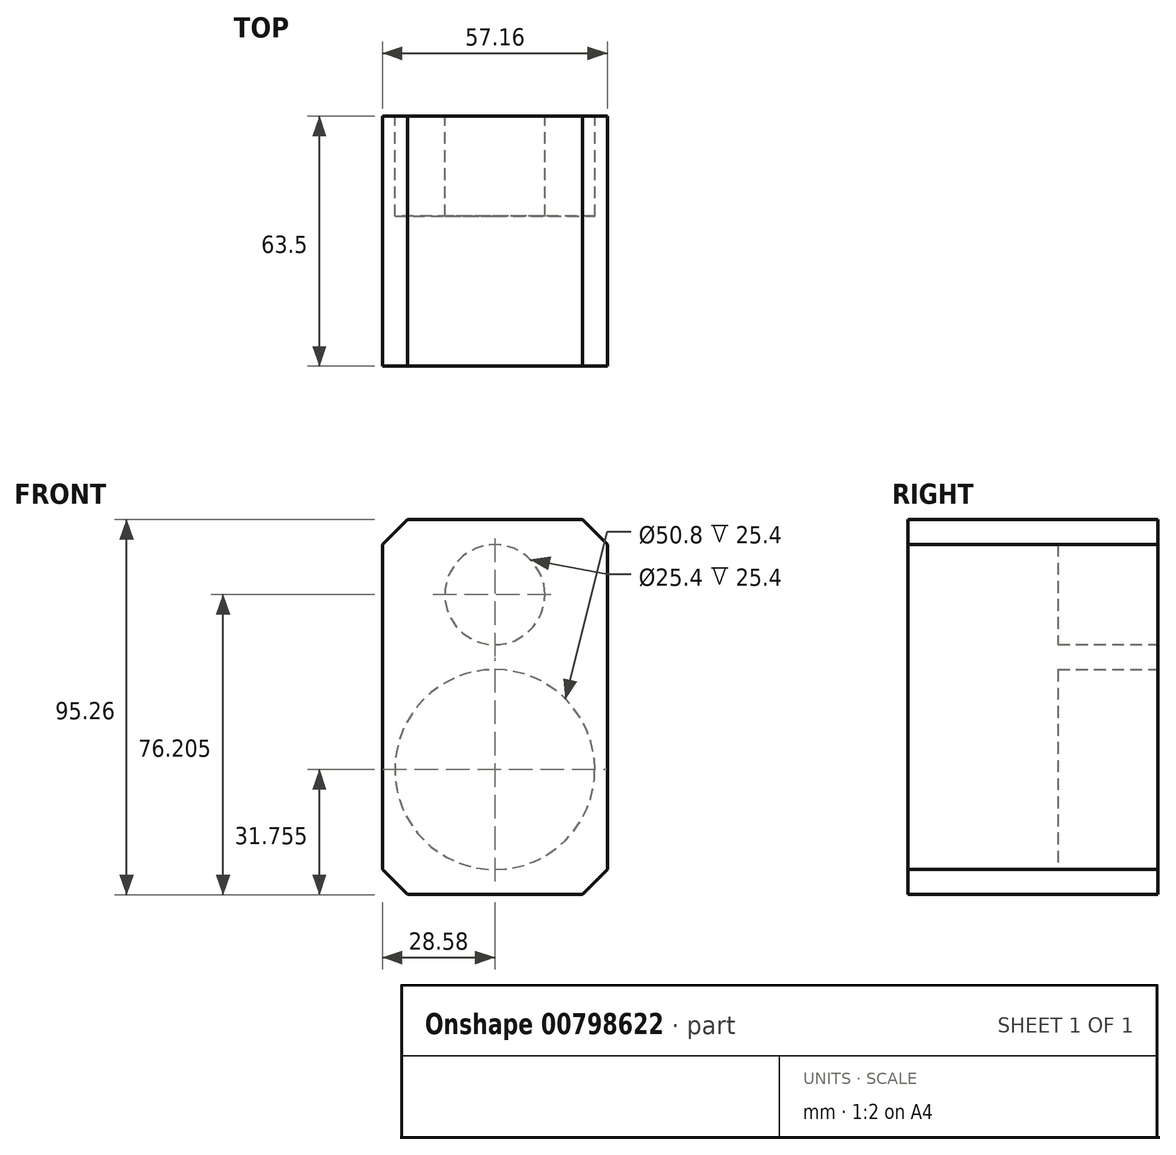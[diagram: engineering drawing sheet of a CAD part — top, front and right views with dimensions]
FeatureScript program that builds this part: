
annotation { "Feature Type Name" : "Feature", "Feature Type Description" : "" }
export const myFeature = defineFeature(function(context is Context, id is Id, definition is map)
    precondition{}
    {
        {
            var Q0;
            Q0=qCreatedBy(makeId("Front.planeOp"),FACE);
            var sketch = newSketch(context, id + "F0", { "sketchPlane" : qUnion([Q0])});
            skLineSegment(sketch, "E0.bottom", {"start": v(28.58, 47.63) * mm, "end": v(-28.58, 47.63) * mm});
            skLineSegment(sketch, "E0.top", {"start": v(28.58, -47.62) * mm, "end": v(-28.58, -47.62) * mm});
            skLineSegment(sketch, "E0.left", {"start": v(28.58, 47.63) * mm, "end": v(28.58, -47.62) * mm});
            skLineSegment(sketch, "E0.right", {"start": v(-28.58, 47.63) * mm, "end": v(-28.58, -47.62) * mm});
            skPoint(sketch, "E0.middle", {"position": v(0, 0) * mm});
            skSolve(sketch);
        }
        {
            var Q0;
            Q0 = qSketchRegion(id + "F0", true);
            extrude(context, id + "F1", {"entities" : qUnion([Q0]), "depth" : 63.5 * mm, "offsetDistance" : 25.4 * mm});
        }
        {
            var Q0;
            Q0=makeQuery(id+"F1.opExtrude","CAP_FACE",FACE,{"disambiguationData":[OSD([sQuery(id+"F0.wireOp",EDGE,"E0.bottom"),sQuery(id+"F0.wireOp",EDGE,"E0.top"),sQuery(id+"F0.wireOp",EDGE,"E0.left"),sQuery(id+"F0.wireOp",EDGE,"E0.right")])],"isStart":true});
            var sketch = newSketch(context, id + "F2", { "sketchPlane" : qUnion([Q0])});
            skCircle(sketch, "E1", {"center": v(0, 28.58) * mm, "radius": 12.7 * mm});
            skCircle(sketch, "E2", {"center": v(0, -15.88) * mm, "radius": 25.4 * mm});
            skSolve(sketch);
        }
        {
            var Q0;
            Q0 = qSketchRegion(id + "F2", true);
            extrude(context, id + "F3", {"entities" : qUnion([Q0]), "operationType" : NewBodyOperationType.REMOVE, "oppositeDirection" : true, "depth" : 25.4 * mm, "offsetDistance" : 25.4 * mm});
        }
        {
            var Q0;
            Q0=makeQuery(id+"F1.opExtrude","SWEPT_EDGE",EDGE,{"disambiguationData":[OSD([sQuery(id+"F0.wireOp",EDGE,"E0.bottom"),sQuery(id+"F0.wireOp",EDGE,"E0.right")])]});
            var Q1;
            Q1=makeQuery(id+"F1.opExtrude","SWEPT_EDGE",EDGE,{"disambiguationData":[OSD([sQuery(id+"F0.wireOp",EDGE,"E0.bottom"),sQuery(id+"F0.wireOp",EDGE,"E0.left")])]});
            var Q2;
            Q2=makeQuery(id+"F1.opExtrude","SWEPT_EDGE",EDGE,{"disambiguationData":[OSD([sQuery(id+"F0.wireOp",EDGE,"E0.top"),sQuery(id+"F0.wireOp",EDGE,"E0.left")])]});
            var Q3;
            Q3=makeQuery(id+"F1.opExtrude","SWEPT_EDGE",EDGE,{"disambiguationData":[OSD([sQuery(id+"F0.wireOp",EDGE,"E0.top"),sQuery(id+"F0.wireOp",EDGE,"E0.right")])]});
            chamfer(context, id + "F4", {"entities" : qUnion([Q0, Q1, Q2, Q3]), "width" : 6.35 * mm, "tangentPropagation" : true});
        }
    });
